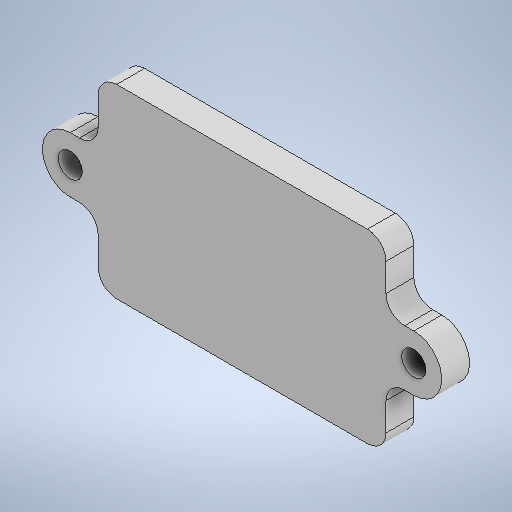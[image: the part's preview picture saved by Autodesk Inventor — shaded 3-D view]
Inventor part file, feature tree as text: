
AUTODESK INVENTOR PART (.ipt)
format: ipt  version: 2025.1 (Build 291241000, 241)  size: 254,976 bytes
history: native  units: mm
features: other x1, extrude x1, fillet x1, sketch x1
ambient origin geometry x8: Origin, YZ Plane, XZ Plane, XY Plane, X Axis, Y Axis, Z Axis, Center Point
bodies: Body1 (feature_tree)
feature tree (4):
  other  "ソリッド1"
  extrude  "押し出し1"  Depth=2.6mm
  fillet  "フィレット1"  Radius=18.5mm
  sketch  "スケッチ1"
